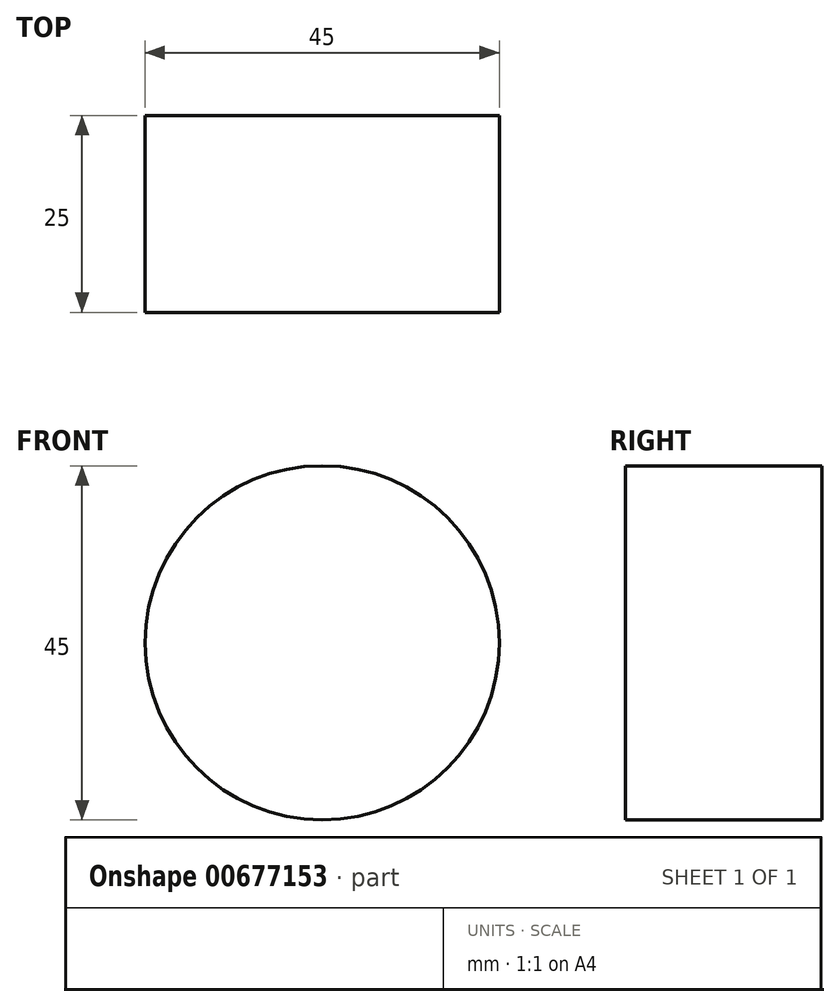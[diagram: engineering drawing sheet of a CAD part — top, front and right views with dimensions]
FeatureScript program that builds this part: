
annotation { "Feature Type Name" : "Feature", "Feature Type Description" : "" }
export const myFeature = defineFeature(function(context is Context, id is Id, definition is map)
    precondition{}
    {
        {
            var Q0;
            Q0=qCreatedBy(makeId("Front.planeOp"),FACE);
            var sketch = newSketch(context, id + "F0", { "sketchPlane" : qUnion([Q0])});
            skCircle(sketch, "E0", {"center": v(0, 0) * mm, "radius": 22.5 * mm});
            skSolve(sketch);
        }
        {
            var Q0;
            Q0=makeQuery(id+"F0.imprint","IMPRINT",FACE,{"disambiguationData":[TD([[makeQuery(id+"F0.imprint","IMPRINT",EDGE,{"derivedFrom":sQuery(id+"F0.wireOp",EDGE,"E0")}),1.0]])]});
            extrude(context, id + "F1", {"entities" : qUnion([Q0]), "depth" : 25 * mm, "offsetDistance" : 25 * mm});
        }
    });
